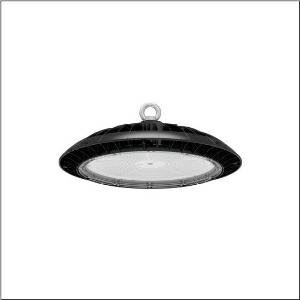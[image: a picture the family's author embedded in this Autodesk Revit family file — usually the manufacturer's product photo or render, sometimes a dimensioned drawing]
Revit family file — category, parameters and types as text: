
# Revit family: highbay_42-l_51hp32mb7mma
name_source: partatom
category: Lighting Fixtures
units: mm (PartAtom-declared; Revit-internal decimal feet)

## family parameters
Cut with Voids When Loaded = No
Host = Face
Light Source = No
Part Type = Normal
Room Calculation Point = No
Round Connector Dimension = Use Diameter
Shared = No

## types (1)
- --- (1 x LED, 28000 lm, 175 W, 5700K)
    Apparent Load = 175 VA
    CIE Flux Codes = 49 82 98 100 100
    Color Rendering = 80
    Color Temperature = 5700K
    Default Elevation = 1800 mm
    Description = Highbay 42-L, high bay luminaire, primary light control with lens, of PC, primary optical cover: cover panel, of PC, transparent, light emission: direct distribution, primary light characteristic: rotationally symmetric, installation type: suspended mounting, surface-mounted, LED, rated luminous flux: 28.000lm, luminous efficacy: 160lm/W, light colour: 857, colour temperature: 5700K, control gear: ON/OFF Multilumen, with cable, 3x 1.0mm², free wire ends, mains connection: 230V, AC, 50Hz, cable length: 1,5m, rated input power: 175W, housing, rotationally symmetric, of diecast aluminium, black, with hook on luminaire side, diameter: 305mm, height: 117mm, protection rating (complete): IP65, insulation class (complete): insulation class I (protective earthing), certification: CE, UKCA, protection symbol: D, impact resistance: IK08, permissible operating ambient temperature: -20..+40°C, corresponds to IFS (International Featured Standards) requirements for safety and quality in the food industry, packaging unit: 1 piece
    Height = 117 mm
    Lamp = 1 x LED
    Lamp Light Flux = 28000 lm
    Lamp Power = 175 W
    Lamp count = 1
    Length = 305 mm
    Luminous efficacy = 160 lm/W
    Manufacturer = Siteco
    ModVariant = No
    Model = 51HP32MB7MMA
    Mounting Place = Ceiling
    Mounting Type = Pendant
    Number of Poles = 1
    OnlyDefault = Yes
    Power Factor = 1
    Product Name = Highbay 42-L
    Product group = high bay luminaire
    ProductGroupID = 902
    Protection Class = Protection class I
    Protection Degree = IP 65
    RLX_Detail_Level = 1
    RLX_Emergency_Light_Flux = 0 lm
    RLX_Emergency_Type = 0
    RLX_Emergency_Type_DB = No
    RlxData = <blob elided: 286353 chars, md5=995b0b5e>
    Socket = socket
    Standby Power = 0 W
    System Light Flux = 28000 lm
    System Power = 175 W
    Type Comments = factory setting: luminous flux: 100 % | (OFF | OFF | OFF)
    Type Image = l_1003932.jpg
    URL = http://relux.com
    VarID = @adj_194957
    Voltage = 0 V
    Weight = 0.00 kg
    Width = 0 mm  [stored 0 ft]

note: [stored X ft] marks values corroborated as IEEE doubles in the binary element streams (Revit-internal decimal feet)

## geometry (parser evidence)
native form markers: Blend x4, Sweep x11
no freeform markers — native parametric forms only
